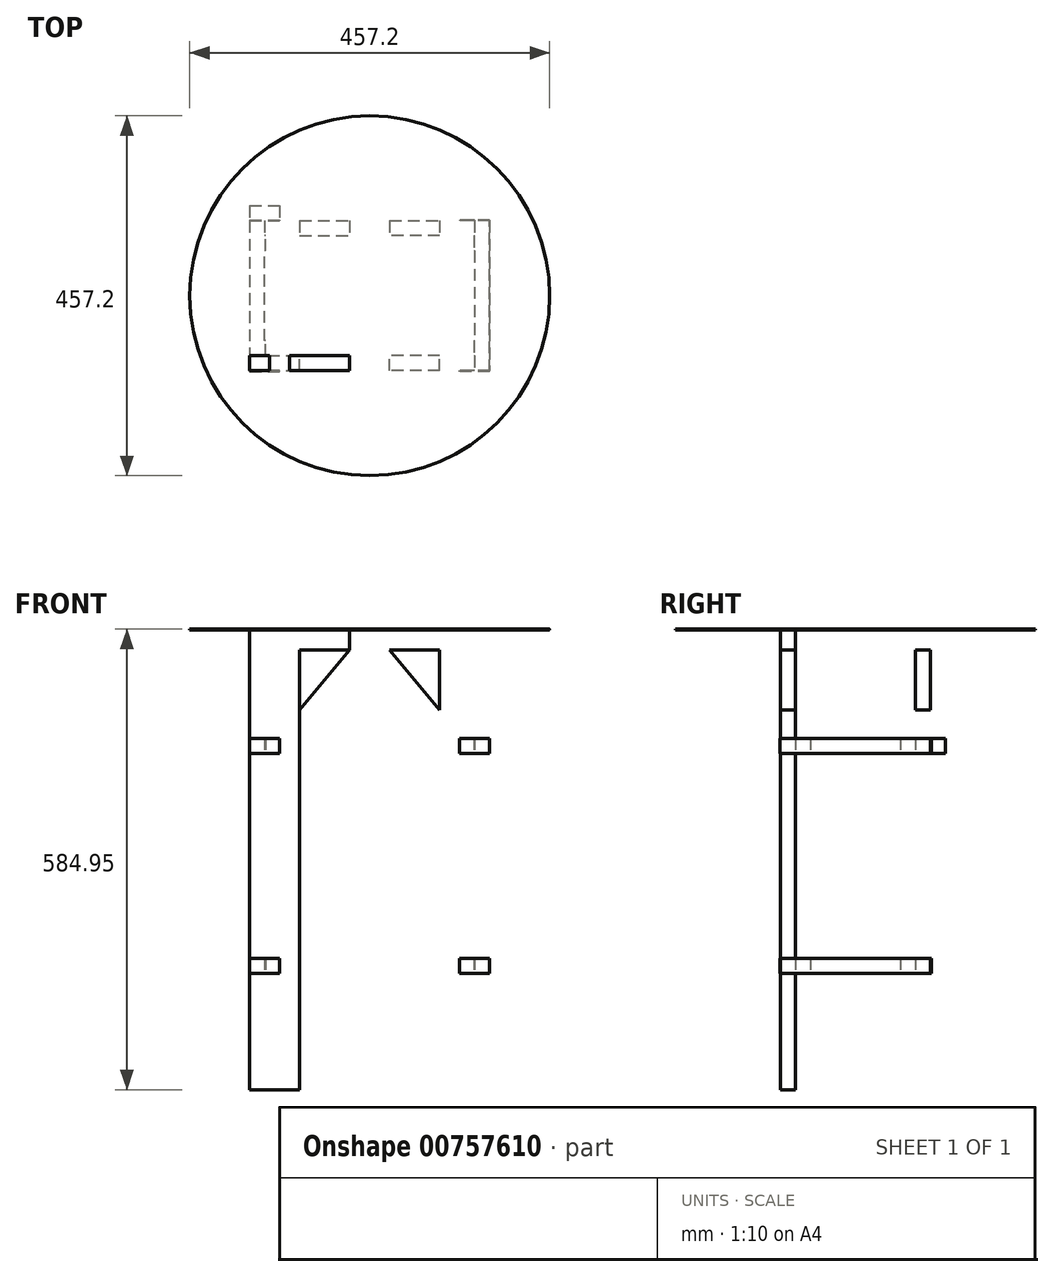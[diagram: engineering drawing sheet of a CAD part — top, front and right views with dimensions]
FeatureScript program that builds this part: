
annotation { "Feature Type Name" : "Feature", "Feature Type Description" : "" }
export const myFeature = defineFeature(function(context is Context, id is Id, definition is map)
    precondition{}
    {
        {
            var Q0;
            Q0=qCreatedBy(makeId("Top.planeOp"),FACE);
            var sketch = newSketch(context, id + "F0", { "sketchPlane" : qUnion([Q0])});
            skCircle(sketch, "E0", {"center": v(0, 0) * mm, "radius": 228.6 * mm});
            skSolve(sketch);
        }
        {
            assignVariable(context, id + "F1", {"name" : "thick", "anyValue" : 3 / 4});
        }
        {
            var Q0;
            Q0=makeQuery(id+"F0.imprint","IMPRINT",FACE,{"disambiguationData":[TD([[makeQuery(id+"F0.imprint","IMPRINT",EDGE,{"derivedFrom":sQuery(id+"F0.wireOp",EDGE,"E0")}),1.0]])]});
            extrude(context, id + "F2", {"entities" : qUnion([Q0]), "depth" : (getVariable(context, 'thick')) * mm, "offsetDistance" : 25.4 * mm});
        }
        {
            var Q0;
            Q0=makeQuery(id+"F2.opExtrude","CAP_FACE",FACE,{"disambiguationData":[OSD([sQuery(id+"F0.wireOp",EDGE,"E0")])],"isStart":true});
            var sketch = newSketch(context, id + "F3", { "sketchPlane" : qUnion([Q0])});
            skLineSegment(sketch, "E1", {"start": v(0, 0) * mm, "end": v(228.6, 0) * mm});
            skLineSegment(sketch, "E2", {"start": v(0, 0) * mm, "end": v(-228.6, 0) * mm});
            skLineSegment(sketch, "E3", {"start": v(0, 0) * mm, "end": v(0, 228.6) * mm});
            skLineSegment(sketch, "E4", {"start": v(0, 0) * mm, "end": v(0, -228.6) * mm});
            skLineSegment(sketch, "E5", {"start": v(-25.4, 76.2) * mm, "end": v(-101.6, 76.2) * mm});
            skLineSegment(sketch, "E6", {"start": v(-127, 76.2) * mm, "end": v(-152.4, 76.2) * mm});
            skLineSegment(sketch, "E7", {"start": v(-152.4, 76.2) * mm, "end": v(-152.4, 95.25) * mm});
            skLineSegment(sketch, "E8", {"start": v(-152.4, 95.25) * mm, "end": v(-127, 95.25) * mm});
            skLineSegment(sketch, "E9", {"start": v(-127, 95.25) * mm, "end": v(-127, 76.2) * mm});
            skLineSegment(sketch, "E10", {"start": v(-101.6, 76.2) * mm, "end": v(-101.6, 95.25) * mm});
            skLineSegment(sketch, "E11", {"start": v(-101.6, 95.25) * mm, "end": v(-25.4, 95.25) * mm});
            skLineSegment(sketch, "E12", {"start": v(-25.4, 95.25) * mm, "end": v(-25.4, 76.2) * mm});
            skLineSegment(sketch, "E13", {"start": v(-127, 76.2) * mm, "end": v(-101.6, 76.2) * mm});
            skLineSegment(sketch, "E14", {"start": v(-101.6, 95.25) * mm, "end": v(-127, 95.25) * mm});
            skSolve(sketch);
        }
        {
            var Q0;
            Q0=makeQuery(id+"F3.imprint","IMPRINT",FACE,{"disambiguationData":[TD([[makeQuery(id+"F3.imprint","IMPRINT",EDGE,{"derivedFrom":sQuery(id+"F3.wireOp",EDGE,"E6")}),-1.0]])]});
            var Q1;
            Q1=makeQuery(id+"F3.imprint","IMPRINT",FACE,{"disambiguationData":[TD([[makeQuery(id+"F3.imprint","IMPRINT",EDGE,{"derivedFrom":sQuery(id+"F3.wireOp",EDGE,"E5")}),-1.0]])]});
            extrude(context, id + "F4", {"entities" : qUnion([Q0, Q1]), "oppositeDirection" : true, "depth" : (getVariable(context, 'thick')) * mm, "offsetDistance" : 25.4 * mm});
        }
        {
            var Q0;
            Q0=makeQuery(id+"F2.opExtrude","CAP_FACE",FACE,{"disambiguationData":[OSD([sQuery(id+"F0.wireOp",EDGE,"E0")])],"isStart":true});
            var sketch = newSketch(context, id + "F5", { "sketchPlane" : qUnion([Q0])});
            skLineSegment(sketch, "E15.bottom", {"start": v(-152.4, 95.25) * mm, "end": v(-25.4, 95.25) * mm});
            skLineSegment(sketch, "E15.top", {"start": v(-152.4, 76.2) * mm, "end": v(-25.4, 76.2) * mm});
            skLineSegment(sketch, "E15.left", {"start": v(-152.4, 95.25) * mm, "end": v(-152.4, 76.2) * mm});
            skLineSegment(sketch, "E15.right", {"start": v(-25.4, 95.25) * mm, "end": v(-25.4, 76.2) * mm});
            skSolve(sketch);
        }
        {
            var Q0;
            Q0=makeQuery(id+"F5.imprint","IMPRINT",FACE,{"disambiguationData":[TD([[makeQuery(id+"F5.imprint","IMPRINT",EDGE,{"derivedFrom":sQuery(id+"F5.wireOp",EDGE,"E15.bottom")}),-1.0]])]});
            extrude(context, id + "F6", {"entities" : qUnion([Q0]), "depth" : 25.4 * mm, "offsetDistance" : 25.4 * mm});
        }
        {
            var Q0;
            Q0=makeQuery(id+"F6.opExtrude","CAP_FACE",FACE,{"disambiguationData":[OSD([sQuery(id+"F5.wireOp",EDGE,"E15.bottom"),sQuery(id+"F5.wireOp",EDGE,"E15.top"),sQuery(id+"F5.wireOp",EDGE,"E15.left"),sQuery(id+"F5.wireOp",EDGE,"E15.right")])],"isStart":false});
            var sketch = newSketch(context, id + "F7", { "sketchPlane" : qUnion([Q0])});
            skLineSegment(sketch, "E16.bottom", {"start": v(-152.4, 95.25) * mm, "end": v(-88.9, 95.25) * mm});
            skLineSegment(sketch, "E16.top", {"start": v(-152.4, 76.2) * mm, "end": v(-88.9, 76.2) * mm});
            skLineSegment(sketch, "E16.left", {"start": v(-152.4, 95.25) * mm, "end": v(-152.4, 76.2) * mm});
            skLineSegment(sketch, "E16.right", {"start": v(-88.9, 95.25) * mm, "end": v(-88.9, 76.2) * mm});
            skSolve(sketch);
        }
        {
            var Q0;
            Q0=makeQuery(id+"F7.imprint","IMPRINT",FACE,{"disambiguationData":[TD([[makeQuery(id+"F7.imprint","IMPRINT",EDGE,{"derivedFrom":sQuery(id+"F7.wireOp",EDGE,"E16.bottom")}),-1.0]])]});
            extrude(context, id + "F8", {"entities" : qUnion([Q0]), "operationType" : NewBodyOperationType.ADD, "depth" : 558.8 * mm, "offsetDistance" : 25.4 * mm});
        }
        {
            var Q0;
            Q0=makeQuery(id+"F6.opExtrude","CAP_FACE",FACE,{"disambiguationData":[OSD([sQuery(id+"F5.wireOp",EDGE,"E15.bottom"),sQuery(id+"F5.wireOp",EDGE,"E15.top"),sQuery(id+"F5.wireOp",EDGE,"E15.left"),sQuery(id+"F5.wireOp",EDGE,"E15.right")])],"isStart":false});
            extrude(context, id + "F9", {"entities" : qUnion([Q0]), "depth" : 76.2 * mm, "offsetDistance" : 25.4 * mm});
        }
        {
            var Q0;
            Q0=makeQuery(id+"F9.opExtrude","CAP_EDGE",EDGE,{"disambiguationData":[OSD([sQuery(id+"F5.wireOp",EDGE,"E15.right")])],"isStart":false});
            chamfer(context, id + "F10", {"entities" : qUnion([Q0]), "chamferType" : ChamferType.TWO_OFFSETS, "width1" : 76.2 * mm, "oppositeDirection" : false, "width2" : 63.5 * mm, "tangentPropagation" : true});
        }
        {
            var Q0;
            Q0=makeQuery(id+"F9.opExtrude","SWEPT_BODY",BODY,{"disambiguationData":[OSD([sQuery(id+"F5.wireOp",EDGE,"E15.bottom"),sQuery(id+"F5.wireOp",EDGE,"E15.top"),sQuery(id+"F5.wireOp",EDGE,"E15.left"),sQuery(id+"F5.wireOp",EDGE,"E15.right")])]});
            var Q1;
            Q1=makeQuery(id+"F4.opExtrude","SWEPT_BODY",BODY,{"disambiguationData":[OSD([sQuery(id+"F3.wireOp",EDGE,"E6"),sQuery(id+"F3.wireOp",EDGE,"E7"),sQuery(id+"F3.wireOp",EDGE,"E8"),sQuery(id+"F3.wireOp",EDGE,"E9")])]});
            booleanBodies(context, id + "F11", {"operationType" : BooleanOperationType.UNION, "tools" : qUnion([Q0, Q1])});
        }
        {
            var Q0;
            Q0=makeQuery(id+"F9.opExtrude","SWEPT_BODY",BODY,{"disambiguationData":[OSD([sQuery(id+"F5.wireOp",EDGE,"E15.bottom"),sQuery(id+"F5.wireOp",EDGE,"E15.top"),sQuery(id+"F5.wireOp",EDGE,"E15.left"),sQuery(id+"F5.wireOp",EDGE,"E15.right")])]});
            var Q1;
            Q1=qCreatedBy(makeId("Right.planeOp"),FACE);
            mirror(context, id + "F12", {"entities" : qUnion([Q0]), "mirrorPlane" : qUnion([Q1])});
        }
        {
            var Q0;
            Q0=makeQuery(id+"F12.opPattern","COPY",BODY,{"derivedFrom":makeQuery(id+"F9.opExtrude","SWEPT_BODY",BODY,{"disambiguationData":[OSD([sQuery(id+"F5.wireOp",EDGE,"E15.bottom"),sQuery(id+"F5.wireOp",EDGE,"E15.top"),sQuery(id+"F5.wireOp",EDGE,"E15.left"),sQuery(id+"F5.wireOp",EDGE,"E15.right")])]}),"instanceName":"1"});
            var Q1;
            Q1=qCreatedBy(makeId("Front.planeOp"),FACE);
            mirror(context, id + "F13", {"entities" : qUnion([Q0]), "mirrorPlane" : qUnion([Q1])});
        }
        {
            var Q0;
            Q0=makeQuery(id+"F13.opPattern","COPY",BODY,{"derivedFrom":makeQuery(id+"F12.opPattern","COPY",BODY,{"derivedFrom":makeQuery(id+"F9.opExtrude","SWEPT_BODY",BODY,{"disambiguationData":[OSD([sQuery(id+"F5.wireOp",EDGE,"E15.bottom"),sQuery(id+"F5.wireOp",EDGE,"E15.top"),sQuery(id+"F5.wireOp",EDGE,"E15.left"),sQuery(id+"F5.wireOp",EDGE,"E15.right")])]}),"instanceName":"1"}),"instanceName":"1"});
            var Q1;
            Q1=qCreatedBy(makeId("Right.planeOp"),FACE);
            mirror(context, id + "F14", {"entities" : qUnion([Q0]), "mirrorPlane" : qUnion([Q1])});
        }
        {
            var Q0;
            {var subQ0=sQuery(id+"F5.wireOp",EDGE,"E15.bottom");Q0=makeQuery(id+"F13.opPattern","COPY",FACE,{"derivedFrom":makeQuery(id+"F12.opPattern","COPY",FACE,{"derivedFrom":makeQuery(id+"F11.opBoolean","MERGE",FACE,{"derivedFrom":[makeQuery(id+"F8.boolean.opBoolean","MERGE",FACE,{"derivedFrom":[makeQuery(id+"F6.opExtrude","SWEPT_FACE",FACE,{"disambiguationData":[OSD([subQ0])]}),makeQuery(id+"F8.opExtrude","SWEPT_FACE",FACE,{"disambiguationData":[OSD([sQuery(id+"F7.wireOp",EDGE,"E16.bottom")])]})]}),makeQuery(id+"F9.opExtrude","SWEPT_FACE",FACE,{"disambiguationData":[OSD([subQ0])]})]}),"instanceName":"1"}),"instanceName":"1"});}
            var sketch = newSketch(context, id + "F15", { "sketchPlane" : qUnion([Q0])});
            skLineSegment(sketch, "E17", {"start": v(-152.4, -137.93) * mm, "end": v(-133.35, -137.93) * mm});
            skLineSegment(sketch, "E18", {"start": v(-133.35, -137.93) * mm, "end": v(-133.35, -156.98) * mm});
            skLineSegment(sketch, "E19", {"start": v(-133.35, -156.98) * mm, "end": v(-152.4, -156.98) * mm});
            skLineSegment(sketch, "E20", {"start": v(-152.4, -156.98) * mm, "end": v(-152.4, -137.93) * mm});
            skSolve(sketch);
        }
        {
            var Q0;
            Q0 = qSketchRegion(id + "F15", true);
            extrude(context, id + "F16", {"entities" : qUnion([Q0]), "oppositeDirection" : true, "depth" : 190.5 * mm, "offsetDistance" : 25.4 * mm});
        }
        {
            var Q0;
            Q0=makeQuery(id+"F12.opPattern","COPY",BODY,{"derivedFrom":makeQuery(id+"F9.opExtrude","SWEPT_BODY",BODY,{"disambiguationData":[OSD([sQuery(id+"F5.wireOp",EDGE,"E15.bottom"),sQuery(id+"F5.wireOp",EDGE,"E15.top"),sQuery(id+"F5.wireOp",EDGE,"E15.left"),sQuery(id+"F5.wireOp",EDGE,"E15.right")])]}),"instanceName":"1"});
            var Q1;
            Q1=makeQuery(id+"F9.opExtrude","SWEPT_BODY",BODY,{"disambiguationData":[OSD([sQuery(id+"F5.wireOp",EDGE,"E15.bottom"),sQuery(id+"F5.wireOp",EDGE,"E15.top"),sQuery(id+"F5.wireOp",EDGE,"E15.left"),sQuery(id+"F5.wireOp",EDGE,"E15.right")])]});
            var Q2;
            Q2=makeQuery(id+"F13.opPattern","COPY",BODY,{"derivedFrom":makeQuery(id+"F12.opPattern","COPY",BODY,{"derivedFrom":makeQuery(id+"F9.opExtrude","SWEPT_BODY",BODY,{"disambiguationData":[OSD([sQuery(id+"F5.wireOp",EDGE,"E15.bottom"),sQuery(id+"F5.wireOp",EDGE,"E15.top"),sQuery(id+"F5.wireOp",EDGE,"E15.left"),sQuery(id+"F5.wireOp",EDGE,"E15.right")])]}),"instanceName":"1"}),"instanceName":"1"});
            var Q3;
            Q3=makeQuery(id+"F14.opPattern","COPY",BODY,{"derivedFrom":makeQuery(id+"F13.opPattern","COPY",BODY,{"derivedFrom":makeQuery(id+"F12.opPattern","COPY",BODY,{"derivedFrom":makeQuery(id+"F9.opExtrude","SWEPT_BODY",BODY,{"disambiguationData":[OSD([sQuery(id+"F5.wireOp",EDGE,"E15.bottom"),sQuery(id+"F5.wireOp",EDGE,"E15.top"),sQuery(id+"F5.wireOp",EDGE,"E15.left"),sQuery(id+"F5.wireOp",EDGE,"E15.right")])]}),"instanceName":"1"}),"instanceName":"1"}),"instanceName":"1"});
            var Q4;
            Q4=makeQuery(id+"F2.opExtrude","SWEPT_BODY",BODY,{"disambiguationData":[OSD([sQuery(id+"F0.wireOp",EDGE,"E0")])]});
            booleanBodies(context, id + "F17", {"operationType" : BooleanOperationType.SUBTRACTION, "tools" : qUnion([Q0, Q1, Q2, Q3]), "targets" : qUnion([Q4]), "keepTools" : true});
        }
        {
            var Q0;
            Q0=makeQuery(id+"F16.opExtrude","SWEPT_BODY",BODY,{"disambiguationData":[OSD([sQuery(id+"F15.wireOp",EDGE,"E17"),sQuery(id+"F15.wireOp",EDGE,"E18"),sQuery(id+"F15.wireOp",EDGE,"E19"),sQuery(id+"F15.wireOp",EDGE,"E20")])]});
            var Q1;
            Q1=makeQuery(id+"F12.opPattern","COPY",BODY,{"derivedFrom":makeQuery(id+"F9.opExtrude","SWEPT_BODY",BODY,{"disambiguationData":[OSD([sQuery(id+"F5.wireOp",EDGE,"E15.bottom"),sQuery(id+"F5.wireOp",EDGE,"E15.top"),sQuery(id+"F5.wireOp",EDGE,"E15.left"),sQuery(id+"F5.wireOp",EDGE,"E15.right")])]}),"instanceName":"1"});
            var Q2;
            Q2=makeQuery(id+"F13.opPattern","COPY",BODY,{"derivedFrom":makeQuery(id+"F12.opPattern","COPY",BODY,{"derivedFrom":makeQuery(id+"F9.opExtrude","SWEPT_BODY",BODY,{"disambiguationData":[OSD([sQuery(id+"F5.wireOp",EDGE,"E15.bottom"),sQuery(id+"F5.wireOp",EDGE,"E15.top"),sQuery(id+"F5.wireOp",EDGE,"E15.left"),sQuery(id+"F5.wireOp",EDGE,"E15.right")])]}),"instanceName":"1"}),"instanceName":"1"});
            booleanBodies(context, id + "F18", {"operationType" : BooleanOperationType.SUBTRACTION, "tools" : qUnion([Q0]), "targets" : qUnion([Q1, Q2]), "keepTools" : true});
        }
        {
            var Q0;
            Q0=makeQuery(id+"F16.opExtrude","SWEPT_BODY",BODY,{"disambiguationData":[OSD([sQuery(id+"F15.wireOp",EDGE,"E17"),sQuery(id+"F15.wireOp",EDGE,"E18"),sQuery(id+"F15.wireOp",EDGE,"E19"),sQuery(id+"F15.wireOp",EDGE,"E20")])]});
            var Q1;
            Q1=qCreatedBy(makeId("Right.planeOp"),FACE);
            mirror(context, id + "F19", {"entities" : qUnion([Q0]), "mirrorPlane" : qUnion([Q1])});
        }
        {
            var Q0;
            Q0=makeQuery(id+"F19.opPattern","COPY",BODY,{"derivedFrom":makeQuery(id+"F16.opExtrude","SWEPT_BODY",BODY,{"disambiguationData":[OSD([sQuery(id+"F15.wireOp",EDGE,"E17"),sQuery(id+"F15.wireOp",EDGE,"E18"),sQuery(id+"F15.wireOp",EDGE,"E19"),sQuery(id+"F15.wireOp",EDGE,"E20")])]}),"instanceName":"1"});
            var Q1;
            Q1=makeQuery(id+"F14.opPattern","COPY",BODY,{"derivedFrom":makeQuery(id+"F13.opPattern","COPY",BODY,{"derivedFrom":makeQuery(id+"F12.opPattern","COPY",BODY,{"derivedFrom":makeQuery(id+"F9.opExtrude","SWEPT_BODY",BODY,{"disambiguationData":[OSD([sQuery(id+"F5.wireOp",EDGE,"E15.bottom"),sQuery(id+"F5.wireOp",EDGE,"E15.top"),sQuery(id+"F5.wireOp",EDGE,"E15.left"),sQuery(id+"F5.wireOp",EDGE,"E15.right")])]}),"instanceName":"1"}),"instanceName":"1"}),"instanceName":"1"});
            var Q2;
            Q2=makeQuery(id+"F9.opExtrude","SWEPT_BODY",BODY,{"disambiguationData":[OSD([sQuery(id+"F5.wireOp",EDGE,"E15.bottom"),sQuery(id+"F5.wireOp",EDGE,"E15.top"),sQuery(id+"F5.wireOp",EDGE,"E15.left"),sQuery(id+"F5.wireOp",EDGE,"E15.right")])]});
            booleanBodies(context, id + "F20", {"operationType" : BooleanOperationType.SUBTRACTION, "tools" : qUnion([Q0]), "targets" : qUnion([Q1, Q2]), "keepTools" : true});
        }
        {
            var Q0;
            {var subQ0=sQuery(id+"F5.wireOp",EDGE,"E15.bottom");Q0=makeQuery(id+"F11.opBoolean","MERGE",FACE,{"derivedFrom":[makeQuery(id+"F8.boolean.opBoolean","MERGE",FACE,{"derivedFrom":[makeQuery(id+"F6.opExtrude","SWEPT_FACE",FACE,{"disambiguationData":[OSD([subQ0])]}),makeQuery(id+"F8.opExtrude","SWEPT_FACE",FACE,{"disambiguationData":[OSD([sQuery(id+"F7.wireOp",EDGE,"E16.bottom")])]})]}),makeQuery(id+"F9.opExtrude","SWEPT_FACE",FACE,{"disambiguationData":[OSD([subQ0])]})]});}
            var sketch = newSketch(context, id + "F21", { "sketchPlane" : qUnion([Q0])});
            skLineSegment(sketch, "E21", {"start": v(-152.4, -436.38) * mm, "end": v(-133.35, -436.38) * mm});
            skLineSegment(sketch, "E22", {"start": v(-133.35, -436.38) * mm, "end": v(-133.35, -417.33) * mm});
            skLineSegment(sketch, "E23", {"start": v(-133.35, -417.33) * mm, "end": v(-152.4, -417.33) * mm});
            skLineSegment(sketch, "E24", {"start": v(-152.4, -417.33) * mm, "end": v(-152.4, -436.38) * mm});
            skSolve(sketch);
        }
        {
            var Q0;
            Q0=makeQuery(id+"F21.imprint","IMPRINT",FACE,{"disambiguationData":[TD([[makeQuery(id+"F21.imprint","IMPRINT",EDGE,{"derivedFrom":sQuery(id+"F21.wireOp",EDGE,"E21")}),1.0]])]});
            extrude(context, id + "F22", {"entities" : qUnion([Q0]), "oppositeDirection" : true, "depth" : 190.5 * mm, "offsetDistance" : 25.4 * mm});
        }
        {
            var Q0;
            Q0=makeQuery(id+"F22.opExtrude","SWEPT_BODY",BODY,{"disambiguationData":[OSD([sQuery(id+"F21.wireOp",EDGE,"E21"),sQuery(id+"F21.wireOp",EDGE,"E22"),sQuery(id+"F21.wireOp",EDGE,"E23"),sQuery(id+"F21.wireOp",EDGE,"E24")])]});
            var Q1;
            Q1=makeQuery(id+"F14.opPattern","COPY",BODY,{"derivedFrom":makeQuery(id+"F13.opPattern","COPY",BODY,{"derivedFrom":makeQuery(id+"F12.opPattern","COPY",BODY,{"derivedFrom":makeQuery(id+"F9.opExtrude","SWEPT_BODY",BODY,{"disambiguationData":[OSD([sQuery(id+"F5.wireOp",EDGE,"E15.bottom"),sQuery(id+"F5.wireOp",EDGE,"E15.top"),sQuery(id+"F5.wireOp",EDGE,"E15.left"),sQuery(id+"F5.wireOp",EDGE,"E15.right")])]}),"instanceName":"1"}),"instanceName":"1"}),"instanceName":"1"});
            var Q2;
            Q2=makeQuery(id+"F9.opExtrude","SWEPT_BODY",BODY,{"disambiguationData":[OSD([sQuery(id+"F5.wireOp",EDGE,"E15.bottom"),sQuery(id+"F5.wireOp",EDGE,"E15.top"),sQuery(id+"F5.wireOp",EDGE,"E15.left"),sQuery(id+"F5.wireOp",EDGE,"E15.right")])]});
            booleanBodies(context, id + "F23", {"operationType" : BooleanOperationType.SUBTRACTION, "tools" : qUnion([Q0]), "targets" : qUnion([Q1, Q2]), "keepTools" : true});
        }
        {
            var Q0;
            Q0=makeQuery(id+"F22.opExtrude","SWEPT_BODY",BODY,{"disambiguationData":[OSD([sQuery(id+"F21.wireOp",EDGE,"E21"),sQuery(id+"F21.wireOp",EDGE,"E22"),sQuery(id+"F21.wireOp",EDGE,"E23"),sQuery(id+"F21.wireOp",EDGE,"E24")])]});
            var Q1;
            Q1=qCreatedBy(makeId("Right.planeOp"),FACE);
            mirror(context, id + "F24", {"entities" : qUnion([Q0]), "mirrorPlane" : qUnion([Q1])});
        }
        {
            var Q0;
            Q0=makeQuery(id+"F24.opPattern","COPY",BODY,{"derivedFrom":makeQuery(id+"F22.opExtrude","SWEPT_BODY",BODY,{"disambiguationData":[OSD([sQuery(id+"F21.wireOp",EDGE,"E21"),sQuery(id+"F21.wireOp",EDGE,"E22"),sQuery(id+"F21.wireOp",EDGE,"E23"),sQuery(id+"F21.wireOp",EDGE,"E24")])]}),"instanceName":"1"});
            var Q1;
            Q1=makeQuery(id+"F12.opPattern","COPY",BODY,{"derivedFrom":makeQuery(id+"F9.opExtrude","SWEPT_BODY",BODY,{"disambiguationData":[OSD([sQuery(id+"F5.wireOp",EDGE,"E15.bottom"),sQuery(id+"F5.wireOp",EDGE,"E15.top"),sQuery(id+"F5.wireOp",EDGE,"E15.left"),sQuery(id+"F5.wireOp",EDGE,"E15.right")])]}),"instanceName":"1"});
            var Q2;
            Q2=makeQuery(id+"F13.opPattern","COPY",BODY,{"derivedFrom":makeQuery(id+"F12.opPattern","COPY",BODY,{"derivedFrom":makeQuery(id+"F9.opExtrude","SWEPT_BODY",BODY,{"disambiguationData":[OSD([sQuery(id+"F5.wireOp",EDGE,"E15.bottom"),sQuery(id+"F5.wireOp",EDGE,"E15.top"),sQuery(id+"F5.wireOp",EDGE,"E15.left"),sQuery(id+"F5.wireOp",EDGE,"E15.right")])]}),"instanceName":"1"}),"instanceName":"1"});
            booleanBodies(context, id + "F25", {"operationType" : BooleanOperationType.SUBTRACTION, "tools" : qUnion([Q0]), "targets" : qUnion([Q1, Q2]), "keepTools" : true});
        }
        {
            var Q0;
            Q0=makeQuery(id+"F19.opPattern","COPY",FACE,{"derivedFrom":makeQuery(id+"F16.opExtrude","CAP_FACE",FACE,{"disambiguationData":[OSD([sQuery(id+"F15.wireOp",EDGE,"E17"),sQuery(id+"F15.wireOp",EDGE,"E18"),sQuery(id+"F15.wireOp",EDGE,"E19"),sQuery(id+"F15.wireOp",EDGE,"E20")])],"isStart":false}),"instanceName":"1"});
            var sketch = newSketch(context, id + "F26", { "sketchPlane" : qUnion([Q0])});
            skLineSegment(sketch, "E25.bottom", {"start": v(-152.4, -137.93) * mm, "end": v(-114.3, -137.93) * mm});
            skLineSegment(sketch, "E25.top", {"start": v(-152.4, -156.98) * mm, "end": v(-114.3, -156.98) * mm});
            skLineSegment(sketch, "E25.left", {"start": v(-152.4, -137.93) * mm, "end": v(-152.4, -156.98) * mm});
            skLineSegment(sketch, "E25.right", {"start": v(-114.3, -137.93) * mm, "end": v(-114.3, -156.98) * mm});
            skSolve(sketch);
        }
        {
            var Q0;
            {var subQ0=sQuery(id+"F26.wireOp",EDGE,"E25.left");Q0=makeQuery(id+"F26.imprint","IMPRINT",FACE,{"disambiguationData":[TD([[makeQuery(id+"F26.imprint","IMPRINT",EDGE,{"derivedFrom":subQ0}),-1.0]])]});}
            var Q1;
            {var subQ2=sQuery(id+"F26.wireOp",EDGE,"E25.right");Q1=makeQuery(id+"F26.imprint","IMPRINT",FACE,{"disambiguationData":[TD([[makeQuery(id+"F26.imprint","IMPRINT",EDGE,{"derivedFrom":subQ2}),-1.0]])]});}
            extrude(context, id + "F27", {"entities" : qUnion([Q0, Q1]), "operationType" : NewBodyOperationType.ADD, "depth" : (getVariable(context, 'thick')) * mm, "offsetDistance" : 25.4 * mm});
        }
        {
            var Q0;
            Q0=makeQuery(id+"F19.opPattern","COPY",FACE,{"derivedFrom":makeQuery(id+"F16.opExtrude","CAP_FACE",FACE,{"disambiguationData":[OSD([sQuery(id+"F15.wireOp",EDGE,"E17"),sQuery(id+"F15.wireOp",EDGE,"E18"),sQuery(id+"F15.wireOp",EDGE,"E19"),sQuery(id+"F15.wireOp",EDGE,"E20")])],"isStart":true}),"instanceName":"1"});
            var sketch = newSketch(context, id + "F28", { "sketchPlane" : qUnion([Q0])});
            skLineSegment(sketch, "E26.bottom", {"start": v(152.4, -137.93) * mm, "end": v(114.3, -137.93) * mm});
            skLineSegment(sketch, "E26.top", {"start": v(152.4, -156.98) * mm, "end": v(114.3, -156.98) * mm});
            skLineSegment(sketch, "E26.left", {"start": v(152.4, -137.93) * mm, "end": v(152.4, -156.98) * mm});
            skLineSegment(sketch, "E26.right", {"start": v(114.3, -137.93) * mm, "end": v(114.3, -156.98) * mm});
            skSolve(sketch);
        }
        {
            var Q0;
            {var subQ0=sQuery(id+"F28.wireOp",EDGE,"E26.left");Q0=makeQuery(id+"F28.imprint","IMPRINT",FACE,{"disambiguationData":[TD([[makeQuery(id+"F28.imprint","IMPRINT",EDGE,{"derivedFrom":subQ0}),1.0]])]});}
            var Q1;
            {var subQ2=sQuery(id+"F28.wireOp",EDGE,"E26.right");Q1=makeQuery(id+"F28.imprint","IMPRINT",FACE,{"disambiguationData":[TD([[makeQuery(id+"F28.imprint","IMPRINT",EDGE,{"derivedFrom":subQ2}),1.0]])]});}
            extrude(context, id + "F29", {"entities" : qUnion([Q0, Q1]), "depth" : 19.05 * mm, "offsetDistance" : 25.4 * mm});
        }
        {
            var Q0;
            Q0=makeQuery(id+"F16.opExtrude","CAP_FACE",FACE,{"disambiguationData":[OSD([sQuery(id+"F15.wireOp",EDGE,"E17"),sQuery(id+"F15.wireOp",EDGE,"E18"),sQuery(id+"F15.wireOp",EDGE,"E19"),sQuery(id+"F15.wireOp",EDGE,"E20")])],"isStart":true});
            var sketch = newSketch(context, id + "F30", { "sketchPlane" : qUnion([Q0])});
            skLineSegment(sketch, "E27.bottom", {"start": v(-152.4, -137.93) * mm, "end": v(-114.3, -137.93) * mm});
            skLineSegment(sketch, "E27.top", {"start": v(-152.4, -156.98) * mm, "end": v(-114.3, -156.98) * mm});
            skLineSegment(sketch, "E27.left", {"start": v(-152.4, -137.93) * mm, "end": v(-152.4, -156.98) * mm});
            skLineSegment(sketch, "E27.right", {"start": v(-114.3, -137.93) * mm, "end": v(-114.3, -156.98) * mm});
            skSolve(sketch);
        }
        {
            var Q0;
            {var subQ0=sQuery(id+"F30.wireOp",EDGE,"E27.left");Q0=makeQuery(id+"F30.imprint","IMPRINT",FACE,{"disambiguationData":[TD([[makeQuery(id+"F30.imprint","IMPRINT",EDGE,{"derivedFrom":subQ0}),-1.0]])]});}
            var Q1;
            {var subQ2=sQuery(id+"F30.wireOp",EDGE,"E27.right");Q1=makeQuery(id+"F30.imprint","IMPRINT",FACE,{"disambiguationData":[TD([[makeQuery(id+"F30.imprint","IMPRINT",EDGE,{"derivedFrom":subQ2}),-1.0]])]});}
            extrude(context, id + "F31", {"entities" : qUnion([Q0, Q1]), "depth" : (getVariable(context, 'thick')) * mm, "offsetDistance" : 25.4 * mm});
        }
        {
            var Q0;
            Q0=makeQuery(id+"F16.opExtrude","CAP_FACE",FACE,{"disambiguationData":[OSD([sQuery(id+"F15.wireOp",EDGE,"E17"),sQuery(id+"F15.wireOp",EDGE,"E18"),sQuery(id+"F15.wireOp",EDGE,"E19"),sQuery(id+"F15.wireOp",EDGE,"E20")])],"isStart":false});
            var sketch = newSketch(context, id + "F32", { "sketchPlane" : qUnion([Q0])});
            skLineSegment(sketch, "E28.bottom", {"start": v(152.4, -137.93) * mm, "end": v(114.3, -137.93) * mm});
            skLineSegment(sketch, "E28.top", {"start": v(152.4, -156.98) * mm, "end": v(114.3, -156.98) * mm});
            skLineSegment(sketch, "E28.left", {"start": v(152.4, -137.93) * mm, "end": v(152.4, -156.98) * mm});
            skLineSegment(sketch, "E28.right", {"start": v(114.3, -137.93) * mm, "end": v(114.3, -156.98) * mm});
            skSolve(sketch);
        }
        {
            var Q0;
            Q0=makeQuery(id+"F22.opExtrude","CAP_FACE",FACE,{"disambiguationData":[OSD([sQuery(id+"F21.wireOp",EDGE,"E21"),sQuery(id+"F21.wireOp",EDGE,"E22"),sQuery(id+"F21.wireOp",EDGE,"E23"),sQuery(id+"F21.wireOp",EDGE,"E24")])],"isStart":true});
            var sketch = newSketch(context, id + "F33", { "sketchPlane" : qUnion([Q0])});
            skLineSegment(sketch, "E29.bottom", {"start": v(-152.4, -417.33) * mm, "end": v(-114.3, -417.33) * mm});
            skLineSegment(sketch, "E29.top", {"start": v(-152.4, -436.38) * mm, "end": v(-114.3, -436.38) * mm});
            skLineSegment(sketch, "E29.left", {"start": v(-152.4, -417.33) * mm, "end": v(-152.4, -436.38) * mm});
            skLineSegment(sketch, "E29.right", {"start": v(-114.3, -417.33) * mm, "end": v(-114.3, -436.38) * mm});
            skSolve(sketch);
        }
        {
            var Q0;
            {var subQ0=sQuery(id+"F32.wireOp",EDGE,"E28.left");Q0=makeQuery(id+"F32.imprint","IMPRINT",FACE,{"disambiguationData":[TD([[makeQuery(id+"F32.imprint","IMPRINT",EDGE,{"derivedFrom":subQ0}),1.0]])]});}
            var Q1;
            {var subQ2=sQuery(id+"F32.wireOp",EDGE,"E28.right");Q1=makeQuery(id+"F32.imprint","IMPRINT",FACE,{"disambiguationData":[TD([[makeQuery(id+"F32.imprint","IMPRINT",EDGE,{"derivedFrom":subQ2}),1.0]])]});}
            extrude(context, id + "F34", {"entities" : qUnion([Q0, Q1]), "operationType" : NewBodyOperationType.ADD, "depth" : (getVariable(context, 'thick')) * mm, "offsetDistance" : 25.4 * mm});
        }
        {
            var Q0;
            Q0 = qSketchRegion(id + "F33", true);
            extrude(context, id + "F35", {"entities" : qUnion([Q0]), "depth" : (getVariable(context, 'thick')) * mm, "offsetDistance" : 25.4 * mm});
        }
        {
            var Q0;
            Q0=makeQuery(id+"F24.opPattern","COPY",FACE,{"derivedFrom":makeQuery(id+"F22.opExtrude","CAP_FACE",FACE,{"disambiguationData":[OSD([sQuery(id+"F21.wireOp",EDGE,"E21"),sQuery(id+"F21.wireOp",EDGE,"E22"),sQuery(id+"F21.wireOp",EDGE,"E23"),sQuery(id+"F21.wireOp",EDGE,"E24")])],"isStart":true}),"instanceName":"1"});
            var sketch = newSketch(context, id + "F36", { "sketchPlane" : qUnion([Q0])});
            skLineSegment(sketch, "E30.bottom", {"start": v(152.4, -417.33) * mm, "end": v(114.3, -417.33) * mm});
            skLineSegment(sketch, "E30.top", {"start": v(152.4, -436.38) * mm, "end": v(114.3, -436.38) * mm});
            skLineSegment(sketch, "E30.left", {"start": v(152.4, -417.33) * mm, "end": v(152.4, -436.38) * mm});
            skLineSegment(sketch, "E30.right", {"start": v(114.3, -417.33) * mm, "end": v(114.3, -436.38) * mm});
            skSolve(sketch);
        }
        {
            var Q0;
            Q0 = qSketchRegion(id + "F36", true);
            extrude(context, id + "F37", {"entities" : qUnion([Q0]), "depth" : (getVariable(context, 'thick')) * mm, "offsetDistance" : 25.4 * mm});
        }
        {
            var Q0;
            Q0=makeQuery(id+"F24.opPattern","COPY",FACE,{"derivedFrom":makeQuery(id+"F22.opExtrude","CAP_FACE",FACE,{"disambiguationData":[OSD([sQuery(id+"F21.wireOp",EDGE,"E21"),sQuery(id+"F21.wireOp",EDGE,"E22"),sQuery(id+"F21.wireOp",EDGE,"E23"),sQuery(id+"F21.wireOp",EDGE,"E24")])],"isStart":false}),"instanceName":"1"});
            var sketch = newSketch(context, id + "F38", { "sketchPlane" : qUnion([Q0])});
            skLineSegment(sketch, "E31.bottom", {"start": v(-152.4, -417.33) * mm, "end": v(-114.3, -417.33) * mm});
            skLineSegment(sketch, "E31.top", {"start": v(-152.4, -436.38) * mm, "end": v(-114.3, -436.38) * mm});
            skLineSegment(sketch, "E31.left", {"start": v(-152.4, -417.33) * mm, "end": v(-152.4, -436.38) * mm});
            skLineSegment(sketch, "E31.right", {"start": v(-114.3, -417.33) * mm, "end": v(-114.3, -436.38) * mm});
            skSolve(sketch);
        }
        {
            var Q0;
            {var subQ2=sQuery(id+"F38.wireOp",EDGE,"E31.right");Q0=makeQuery(id+"F38.imprint","IMPRINT",FACE,{"disambiguationData":[TD([[makeQuery(id+"F38.imprint","IMPRINT",EDGE,{"derivedFrom":subQ2}),-1.0]])]});}
            var Q1;
            {var subQ2=sQuery(id+"F38.wireOp",EDGE,"E31.left");Q1=makeQuery(id+"F38.imprint","IMPRINT",FACE,{"disambiguationData":[TD([[makeQuery(id+"F38.imprint","IMPRINT",EDGE,{"derivedFrom":subQ2}),1.0]])]});}
            extrude(context, id + "F39", {"entities" : qUnion([Q0, Q1]), "depth" : (getVariable(context, 'thick')) * mm, "offsetDistance" : 25.4 * mm});
        }
        {
            var Q0;
            Q0=makeQuery(id+"F22.opExtrude","CAP_FACE",FACE,{"disambiguationData":[OSD([sQuery(id+"F21.wireOp",EDGE,"E21"),sQuery(id+"F21.wireOp",EDGE,"E22"),sQuery(id+"F21.wireOp",EDGE,"E23"),sQuery(id+"F21.wireOp",EDGE,"E24")])],"isStart":false});
            var sketch = newSketch(context, id + "F40", { "sketchPlane" : qUnion([Q0])});
            skLineSegment(sketch, "E32.bottom", {"start": v(152.4, -417.33) * mm, "end": v(114.3, -417.33) * mm});
            skLineSegment(sketch, "E32.top", {"start": v(152.4, -436.38) * mm, "end": v(114.3, -436.38) * mm});
            skLineSegment(sketch, "E32.left", {"start": v(152.4, -417.33) * mm, "end": v(152.4, -436.38) * mm});
            skLineSegment(sketch, "E32.right", {"start": v(114.3, -417.33) * mm, "end": v(114.3, -436.38) * mm});
            skSolve(sketch);
        }
        {
            var Q0;
            Q0 = qSketchRegion(id + "F40", true);
            extrude(context, id + "F41", {"entities" : qUnion([Q0]), "depth" : (getVariable(context, 'thick')) * mm, "offsetDistance" : 25.4 * mm});
        }
        {
            var Q0;
            Q0=makeQuery(id+"F16.opExtrude","SWEPT_FACE",FACE,{"disambiguationData":[OSD([sQuery(id+"F15.wireOp",EDGE,"E18")])]});
            var sketch = newSketch(context, id + "F42", { "sketchPlane" : qUnion([Q0])});
            skLineSegment(sketch, "E33.right", {"start": v(-76.2, -137.93) * mm, "end": v(-76.2, -156.98) * mm});
            skLineSegment(sketch, "E34.bottom", {"start": v(-76.2, -137.93) * mm, "end": v(-57.15, -137.93) * mm});
            skLineSegment(sketch, "E34.top", {"start": v(-76.2, -156.98) * mm, "end": v(-57.15, -156.98) * mm});
            skLineSegment(sketch, "E34.right", {"start": v(-57.15, -137.93) * mm, "end": v(-57.15, -156.98) * mm});
            skLineSegment(sketch, "E35.right", {"start": v(76.2, -137.93) * mm, "end": v(76.2, -156.98) * mm});
            skLineSegment(sketch, "E36.bottom", {"start": v(76.2, -137.93) * mm, "end": v(57.15, -137.93) * mm});
            skLineSegment(sketch, "E36.top", {"start": v(76.2, -156.98) * mm, "end": v(57.15, -156.98) * mm});
            skLineSegment(sketch, "E36.right", {"start": v(57.15, -137.93) * mm, "end": v(57.15, -156.98) * mm});
            skSolve(sketch);
        }
        {
            var Q0;
            Q0=makeQuery(id+"F42.imprint","IMPRINT",FACE,{"disambiguationData":[TD([[makeQuery(id+"F42.imprint","IMPRINT",EDGE,{"derivedFrom":sQuery(id+"F42.wireOp",EDGE,"E34.bottom")}),1.0]])]});
            var Q1;
            Q1=makeQuery(id+"F42.imprint","IMPRINT",FACE,{"disambiguationData":[TD([[makeQuery(id+"F42.imprint","IMPRINT",EDGE,{"derivedFrom":sQuery(id+"F42.wireOp",EDGE,"E36.bottom")}),1.0]])]});
            extrude(context, id + "F43", {"entities" : qUnion([Q0, Q1]), "operationType" : NewBodyOperationType.ADD, "depth" : (getVariable(context, 'thick')) * mm, "offsetDistance" : 25.4 * mm});
        }
        {
            var Q0;
            Q0=makeQuery(id+"F19.opPattern","COPY",FACE,{"derivedFrom":makeQuery(id+"F16.opExtrude","SWEPT_FACE",FACE,{"disambiguationData":[OSD([sQuery(id+"F15.wireOp",EDGE,"E18")])]}),"instanceName":"1"});
            var sketch = newSketch(context, id + "F44", { "sketchPlane" : qUnion([Q0])});
            skLineSegment(sketch, "E37.right", {"start": v(-76.2, -137.93) * mm, "end": v(-76.2, -156.98) * mm});
            skLineSegment(sketch, "E38.bottom", {"start": v(-76.2, -137.93) * mm, "end": v(-57.15, -137.93) * mm});
            skLineSegment(sketch, "E38.top", {"start": v(-76.2, -156.98) * mm, "end": v(-57.15, -156.98) * mm});
            skLineSegment(sketch, "E38.right", {"start": v(-57.15, -137.93) * mm, "end": v(-57.15, -156.98) * mm});
            skLineSegment(sketch, "E39.right", {"start": v(76.2, -137.93) * mm, "end": v(76.2, -156.98) * mm});
            skLineSegment(sketch, "E40.bottom", {"start": v(76.2, -137.93) * mm, "end": v(57.15, -137.93) * mm});
            skLineSegment(sketch, "E40.top", {"start": v(76.2, -156.98) * mm, "end": v(57.15, -156.98) * mm});
            skLineSegment(sketch, "E40.right", {"start": v(57.15, -137.93) * mm, "end": v(57.15, -156.98) * mm});
            skSolve(sketch);
        }
        {
            var Q0;
            Q0=makeQuery(id+"F44.imprint","IMPRINT",FACE,{"disambiguationData":[TD([[makeQuery(id+"F44.imprint","IMPRINT",EDGE,{"derivedFrom":sQuery(id+"F44.wireOp",EDGE,"E38.bottom")}),-1.0]])]});
            var Q1;
            Q1=makeQuery(id+"F44.imprint","IMPRINT",FACE,{"disambiguationData":[TD([[makeQuery(id+"F44.imprint","IMPRINT",EDGE,{"derivedFrom":sQuery(id+"F44.wireOp",EDGE,"E40.bottom")}),-1.0]])]});
            extrude(context, id + "F45", {"entities" : qUnion([Q0, Q1]), "operationType" : NewBodyOperationType.ADD, "depth" : (getVariable(context, 'thick')) * mm, "offsetDistance" : 25.4 * mm});
        }
        {
            var Q0;
            Q0=makeQuery(id+"F22.opExtrude","SWEPT_FACE",FACE,{"disambiguationData":[OSD([sQuery(id+"F21.wireOp",EDGE,"E22")])]});
            var sketch = newSketch(context, id + "F46", { "sketchPlane" : qUnion([Q0])});
            skLineSegment(sketch, "E41.bottom", {"start": v(-95.25, -417.33) * mm, "end": v(-76.2, -417.33) * mm});
            skLineSegment(sketch, "E41.top", {"start": v(-95.25, -436.38) * mm, "end": v(-76.2, -436.38) * mm});
            skLineSegment(sketch, "E41.left", {"start": v(-95.25, -417.33) * mm, "end": v(-95.25, -436.38) * mm});
            skLineSegment(sketch, "E41.right", {"start": v(-76.2, -417.33) * mm, "end": v(-76.2, -436.38) * mm});
            skLineSegment(sketch, "E42.bottom", {"start": v(-76.2, -417.33) * mm, "end": v(-57.15, -417.33) * mm});
            skLineSegment(sketch, "E42.top", {"start": v(-76.2, -436.38) * mm, "end": v(-57.15, -436.38) * mm});
            skLineSegment(sketch, "E42.right", {"start": v(-57.15, -417.33) * mm, "end": v(-57.15, -436.38) * mm});
            skSolve(sketch);
        }
        {
            var Q0;
            Q0=makeQuery(id+"F46.imprint","IMPRINT",FACE,{"disambiguationData":[TD([[makeQuery(id+"F46.imprint","IMPRINT",EDGE,{"derivedFrom":sQuery(id+"F46.wireOp",EDGE,"E42.bottom")}),1.0]])]});
            extrude(context, id + "F47", {"entities" : qUnion([Q0]), "operationType" : NewBodyOperationType.ADD, "depth" : (getVariable(context, 'thick')) * mm, "offsetDistance" : 25.4 * mm});
        }
        {
            var Q0;
            Q0=makeQuery(id+"F47.boolean.opBoolean","SPLIT",FACE,{"disambiguationData":[TD([makeQuery(id+"F47.opExtrude","SWEPT_FACE",FACE,{"disambiguationData":[OSD([sQuery(id+"F46.wireOp",EDGE,"E42.right")])]})])],"derivedFrom":makeQuery(id+"F22.opExtrude","SWEPT_FACE",FACE,{"disambiguationData":[OSD([sQuery(id+"F21.wireOp",EDGE,"E22")])]})});
            var sketch = newSketch(context, id + "F48", { "sketchPlane" : qUnion([Q0])});
            skLineSegment(sketch, "E43.bottom", {"start": v(95.25, -417.33) * mm, "end": v(76.2, -417.33) * mm});
            skLineSegment(sketch, "E43.top", {"start": v(95.25, -436.38) * mm, "end": v(76.2, -436.38) * mm});
            skLineSegment(sketch, "E43.left", {"start": v(95.25, -417.33) * mm, "end": v(95.25, -436.38) * mm});
            skLineSegment(sketch, "E43.right", {"start": v(76.2, -417.33) * mm, "end": v(76.2, -436.38) * mm});
            skLineSegment(sketch, "E44.bottom", {"start": v(76.2, -417.33) * mm, "end": v(57.15, -417.33) * mm});
            skLineSegment(sketch, "E44.top", {"start": v(76.2, -436.38) * mm, "end": v(57.15, -436.38) * mm});
            skLineSegment(sketch, "E44.right", {"start": v(57.15, -417.33) * mm, "end": v(57.15, -436.38) * mm});
            skSolve(sketch);
        }
        {
            var Q0;
            Q0=makeQuery(id+"F48.imprint","IMPRINT",FACE,{"disambiguationData":[TD([[makeQuery(id+"F48.imprint","IMPRINT",EDGE,{"derivedFrom":sQuery(id+"F48.wireOp",EDGE,"E44.bottom")}),1.0]])]});
            extrude(context, id + "F49", {"entities" : qUnion([Q0]), "operationType" : NewBodyOperationType.ADD, "depth" : (getVariable(context, 'thick')) * mm, "offsetDistance" : 25.4 * mm});
        }
        {
            var Q0;
            Q0=makeQuery(id+"F24.opPattern","COPY",FACE,{"derivedFrom":makeQuery(id+"F22.opExtrude","SWEPT_FACE",FACE,{"disambiguationData":[OSD([sQuery(id+"F21.wireOp",EDGE,"E22")])]}),"instanceName":"1"});
            var sketch = newSketch(context, id + "F50", { "sketchPlane" : qUnion([Q0])});
            skLineSegment(sketch, "E45.right", {"start": v(-76.2, -417.33) * mm, "end": v(-76.2, -436.38) * mm});
            skLineSegment(sketch, "E46.bottom", {"start": v(-76.2, -417.33) * mm, "end": v(-57.15, -417.33) * mm});
            skLineSegment(sketch, "E46.top", {"start": v(-76.2, -436.38) * mm, "end": v(-57.15, -436.38) * mm});
            skLineSegment(sketch, "E46.right", {"start": v(-57.15, -417.33) * mm, "end": v(-57.15, -436.38) * mm});
            skLineSegment(sketch, "E47.right", {"start": v(76.2, -417.33) * mm, "end": v(76.2, -436.38) * mm});
            skLineSegment(sketch, "E48.bottom", {"start": v(76.2, -417.33) * mm, "end": v(57.15, -417.33) * mm});
            skLineSegment(sketch, "E48.top", {"start": v(76.2, -436.38) * mm, "end": v(57.15, -436.38) * mm});
            skLineSegment(sketch, "E48.right", {"start": v(57.15, -417.33) * mm, "end": v(57.15, -436.38) * mm});
            skSolve(sketch);
        }
        {
            var Q0;
            Q0=makeQuery(id+"F50.imprint","IMPRINT",FACE,{"disambiguationData":[TD([[makeQuery(id+"F50.imprint","IMPRINT",EDGE,{"derivedFrom":sQuery(id+"F50.wireOp",EDGE,"E46.bottom")}),-1.0]])]});
            var Q1;
            Q1=makeQuery(id+"F50.imprint","IMPRINT",FACE,{"disambiguationData":[TD([[makeQuery(id+"F50.imprint","IMPRINT",EDGE,{"derivedFrom":sQuery(id+"F50.wireOp",EDGE,"E48.bottom")}),-1.0]])]});
            extrude(context, id + "F51", {"entities" : qUnion([Q0, Q1]), "operationType" : NewBodyOperationType.ADD, "depth" : (getVariable(context, 'thick')) * mm, "offsetDistance" : 25.4 * mm});
        }
    });
